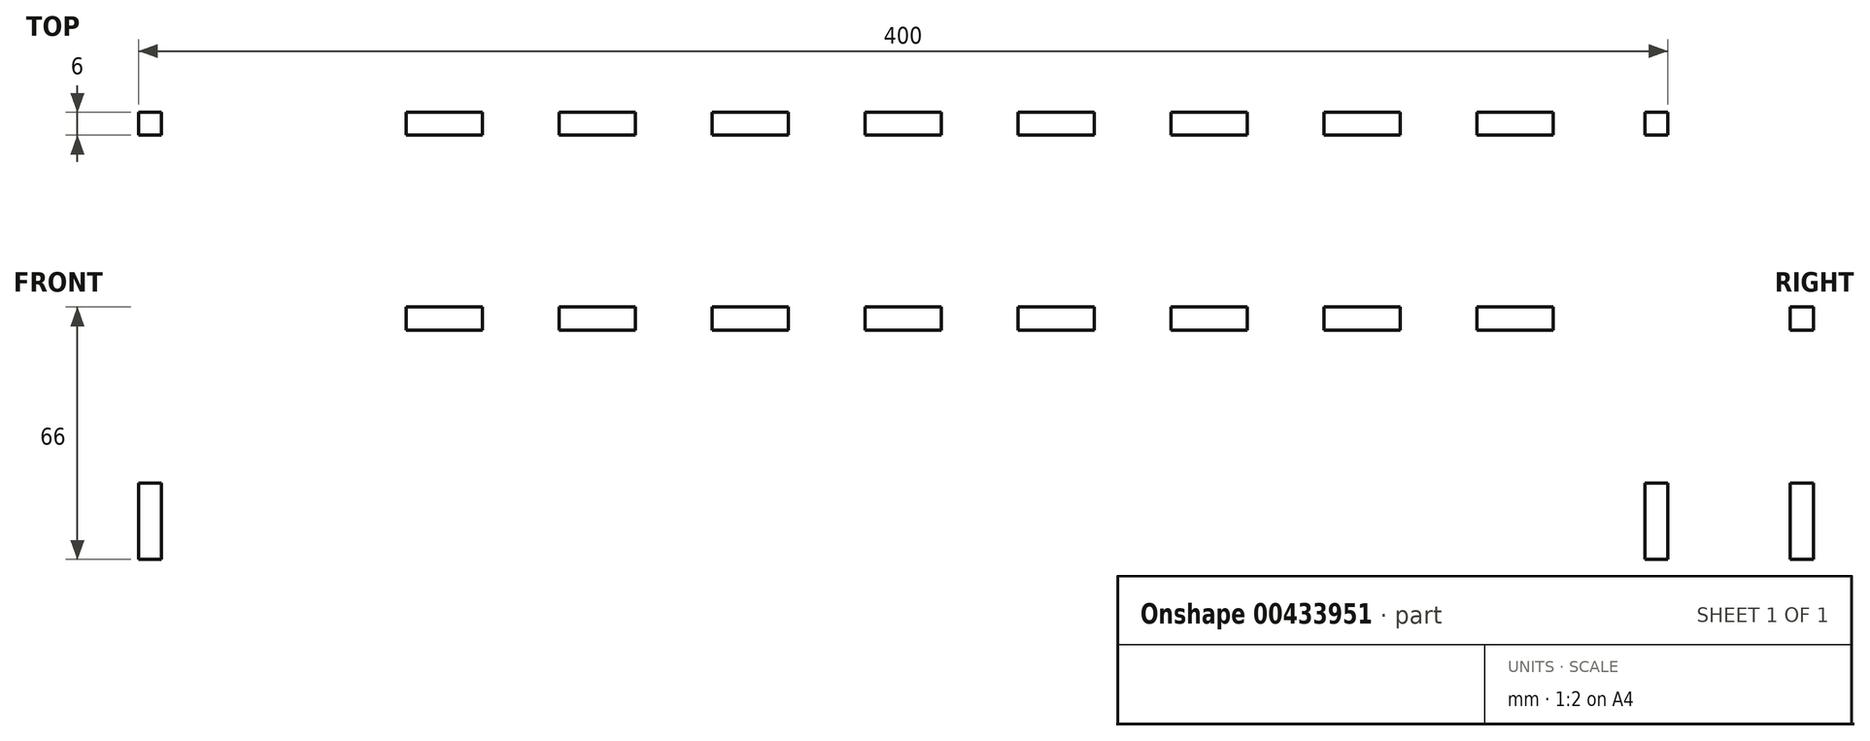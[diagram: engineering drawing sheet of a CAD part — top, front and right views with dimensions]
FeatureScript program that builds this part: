
annotation { "Feature Type Name" : "Feature", "Feature Type Description" : "" }
export const myFeature = defineFeature(function(context is Context, id is Id, definition is map)
    precondition{}
    {
        {
            var Q0;
            Q0=qCreatedBy(makeId("Front.planeOp"),FACE);
            var sketch = newSketch(context, id + "F0", { "sketchPlane" : qUnion([Q0])});
            skLineSegment(sketch, "E0.bottom", {"start": v(200, -30) * mm, "end": v(-200, -30) * mm});
            skLineSegment(sketch, "E0.top", {"start": v(200, 30) * mm, "end": v(-200, 30) * mm});
            skLineSegment(sketch, "E0.left", {"start": v(200, -30) * mm, "end": v(200, 30) * mm});
            skLineSegment(sketch, "E0.right", {"start": v(-200, -30) * mm, "end": v(-200, 30) * mm});
            skPoint(sketch, "E0.middle", {"position": v(0, 0) * mm});
            skLineSegment(sketch, "E1.bottom", {"start": v(-200, 30) * mm, "end": v(-194, 30) * mm});
            skLineSegment(sketch, "E1.top", {"start": v(-200, 10) * mm, "end": v(-194, 10) * mm});
            skLineSegment(sketch, "E1.left", {"start": v(-200, 30) * mm, "end": v(-200, 10) * mm});
            skLineSegment(sketch, "E1.right", {"start": v(-194, 30) * mm, "end": v(-194, 10) * mm});
            skLineSegment(sketch, "E2.MirrorCS", {"start": v(194, 30) * mm, "end": v(194, 10) * mm});
            skLineSegment(sketch, "E3.MirrorCS", {"start": v(200, 30) * mm, "end": v(200, 10) * mm});
            skLineSegment(sketch, "E4.MirrorCS", {"start": v(200, 30) * mm, "end": v(194, 30) * mm});
            skLineSegment(sketch, "E5.MirrorCS", {"start": v(200, 10) * mm, "end": v(194, 10) * mm});
            skLineSegment(sketch, "E6.MirrorCS", {"start": v(-200, -30) * mm, "end": v(-194, -30) * mm});
            skLineSegment(sketch, "E7.MirrorCS", {"start": v(-194, -30) * mm, "end": v(-194, -10) * mm});
            skLineSegment(sketch, "E8.MirrorCS", {"start": v(-200, -30) * mm, "end": v(-200, -10) * mm});
            skLineSegment(sketch, "E9.MirrorCS", {"start": v(-200, -10) * mm, "end": v(-194, -10) * mm});
            skLineSegment(sketch, "E10.bottom", {"start": v(-170, 30) * mm, "end": v(-150, 30) * mm});
            skLineSegment(sketch, "E10.top", {"start": v(-170, 36) * mm, "end": v(-150, 36) * mm});
            skLineSegment(sketch, "E10.left", {"start": v(-170, 30) * mm, "end": v(-170, 36) * mm});
            skLineSegment(sketch, "E10.right", {"start": v(-150, 30) * mm, "end": v(-150, 36) * mm});
            skLineSegment(sketch, "E11.1.0.0", {"start": v(-130, 30) * mm, "end": v(-130, 36) * mm});
            skLineSegment(sketch, "E11.1.0.1", {"start": v(-130, 30) * mm, "end": v(-110, 30) * mm});
            skLineSegment(sketch, "E11.1.0.2", {"start": v(-130, 36) * mm, "end": v(-110, 36) * mm});
            skLineSegment(sketch, "E11.1.0.3", {"start": v(-110, 30) * mm, "end": v(-110, 36) * mm});
            skLineSegment(sketch, "E11.2.0.0", {"start": v(-90, 30) * mm, "end": v(-90, 36) * mm});
            skLineSegment(sketch, "E11.2.0.1", {"start": v(-90, 30) * mm, "end": v(-70, 30) * mm});
            skLineSegment(sketch, "E11.2.0.2", {"start": v(-90, 36) * mm, "end": v(-70, 36) * mm});
            skLineSegment(sketch, "E11.2.0.3", {"start": v(-70, 30) * mm, "end": v(-70, 36) * mm});
            skLineSegment(sketch, "E11.3.0.0", {"start": v(-50, 30) * mm, "end": v(-50, 36) * mm});
            skLineSegment(sketch, "E11.3.0.1", {"start": v(-50, 30) * mm, "end": v(-30, 30) * mm});
            skLineSegment(sketch, "E11.3.0.2", {"start": v(-50, 36) * mm, "end": v(-30, 36) * mm});
            skLineSegment(sketch, "E11.3.0.3", {"start": v(-30, 30) * mm, "end": v(-30, 36) * mm});
            skLineSegment(sketch, "E11.4.0.0", {"start": v(-10, 30) * mm, "end": v(-10, 36) * mm});
            skLineSegment(sketch, "E11.4.0.1", {"start": v(-10, 30) * mm, "end": v(10, 30) * mm});
            skLineSegment(sketch, "E11.4.0.2", {"start": v(-10, 36) * mm, "end": v(10, 36) * mm});
            skLineSegment(sketch, "E11.4.0.3", {"start": v(10, 30) * mm, "end": v(10, 36) * mm});
            skLineSegment(sketch, "E11.5.0.0", {"start": v(30, 30) * mm, "end": v(30, 36) * mm});
            skLineSegment(sketch, "E11.5.0.1", {"start": v(30, 30) * mm, "end": v(50, 30) * mm});
            skLineSegment(sketch, "E11.5.0.2", {"start": v(30, 36) * mm, "end": v(50, 36) * mm});
            skLineSegment(sketch, "E11.5.0.3", {"start": v(50, 30) * mm, "end": v(50, 36) * mm});
            skLineSegment(sketch, "E11.6.0.0", {"start": v(70, 30) * mm, "end": v(70, 36) * mm});
            skLineSegment(sketch, "E11.6.0.1", {"start": v(70, 30) * mm, "end": v(90, 30) * mm});
            skLineSegment(sketch, "E11.6.0.2", {"start": v(70, 36) * mm, "end": v(90, 36) * mm});
            skLineSegment(sketch, "E11.6.0.3", {"start": v(90, 30) * mm, "end": v(90, 36) * mm});
            skLineSegment(sketch, "E11.7.0.0", {"start": v(110, 30) * mm, "end": v(110, 36) * mm});
            skLineSegment(sketch, "E11.7.0.1", {"start": v(110, 30) * mm, "end": v(130, 30) * mm});
            skLineSegment(sketch, "E11.7.0.2", {"start": v(110, 36) * mm, "end": v(130, 36) * mm});
            skLineSegment(sketch, "E11.7.0.3", {"start": v(130, 30) * mm, "end": v(130, 36) * mm});
            skLineSegment(sketch, "E11.8.0.0", {"start": v(150, 30) * mm, "end": v(150, 36) * mm});
            skLineSegment(sketch, "E11.8.0.1", {"start": v(150, 30) * mm, "end": v(170, 30) * mm});
            skLineSegment(sketch, "E11.8.0.2", {"start": v(150, 36) * mm, "end": v(170, 36) * mm});
            skLineSegment(sketch, "E11.8.0.3", {"start": v(170, 30) * mm, "end": v(170, 36) * mm});
            skLineSegment(sketch, "E11.direction1", {"start": v(-170, 30) * mm, "end": v(-130, 30) * mm, "construction": true});
            skLineSegment(sketch, "E12.MirrorCS", {"start": v(200, -10) * mm, "end": v(194, -10) * mm});
            skLineSegment(sketch, "E13.MirrorCS", {"start": v(200, -30) * mm, "end": v(200, -10) * mm});
            skLineSegment(sketch, "E14.MirrorCS", {"start": v(194, -30) * mm, "end": v(194, -10) * mm});
            skLineSegment(sketch, "E15.MirrorCS", {"start": v(200, -30) * mm, "end": v(194, -30) * mm});
            skSolve(sketch);
        }
        {
            var Q0;
            Q0=makeQuery(id+"F0.imprint","IMPRINT",FACE,{"disambiguationData":[TD([[makeQuery(id+"F0.imprint","IMPRINT",EDGE,{"derivedFrom":sQuery(id+"F0.wireOp",EDGE,"E0.bottom")}),-1.0]])]});
            var Q1;
            Q1=makeQuery(id+"F0.imprint","IMPRINT",FACE,{"disambiguationData":[TD([[makeQuery(id+"F0.imprint","IMPRINT",EDGE,{"derivedFrom":sQuery(id+"F0.wireOp",EDGE,"E10.bottom")}),1.0]])]});
            var Q2;
            Q2=makeQuery(id+"F0.imprint","IMPRINT",FACE,{"disambiguationData":[TD([[makeQuery(id+"F0.imprint","IMPRINT",EDGE,{"derivedFrom":sQuery(id+"F0.wireOp",EDGE,"E11.1.0.0")}),-1.0]])]});
            var Q3;
            Q3=makeQuery(id+"F0.imprint","IMPRINT",FACE,{"disambiguationData":[TD([[makeQuery(id+"F0.imprint","IMPRINT",EDGE,{"derivedFrom":sQuery(id+"F0.wireOp",EDGE,"E11.2.0.0")}),-1.0]])]});
            var Q4;
            Q4=makeQuery(id+"F0.imprint","IMPRINT",FACE,{"disambiguationData":[TD([[makeQuery(id+"F0.imprint","IMPRINT",EDGE,{"derivedFrom":sQuery(id+"F0.wireOp",EDGE,"E11.3.0.0")}),-1.0]])]});
            var Q5;
            Q5=makeQuery(id+"F0.imprint","IMPRINT",FACE,{"disambiguationData":[TD([[makeQuery(id+"F0.imprint","IMPRINT",EDGE,{"derivedFrom":sQuery(id+"F0.wireOp",EDGE,"E11.4.0.0")}),-1.0]])]});
            var Q6;
            Q6=makeQuery(id+"F0.imprint","IMPRINT",FACE,{"disambiguationData":[TD([[makeQuery(id+"F0.imprint","IMPRINT",EDGE,{"derivedFrom":sQuery(id+"F0.wireOp",EDGE,"E11.5.0.0")}),-1.0]])]});
            var Q7;
            Q7=makeQuery(id+"F0.imprint","IMPRINT",FACE,{"disambiguationData":[TD([[makeQuery(id+"F0.imprint","IMPRINT",EDGE,{"derivedFrom":sQuery(id+"F0.wireOp",EDGE,"E11.6.0.0")}),-1.0]])]});
            var Q8;
            Q8=makeQuery(id+"F0.imprint","IMPRINT",FACE,{"disambiguationData":[TD([[makeQuery(id+"F0.imprint","IMPRINT",EDGE,{"derivedFrom":sQuery(id+"F0.wireOp",EDGE,"E11.7.0.0")}),-1.0]])]});
            var Q9;
            Q9=makeQuery(id+"F0.imprint","IMPRINT",FACE,{"disambiguationData":[TD([[makeQuery(id+"F0.imprint","IMPRINT",EDGE,{"derivedFrom":sQuery(id+"F0.wireOp",EDGE,"E11.8.0.0")}),-1.0]])]});
            extrude(context, id + "F1", {"entities" : qUnion([Q0, Q1, Q2, Q3, Q4, Q5, Q6, Q7, Q8, Q9]), "depth" : 6 * mm});
        }
    });
